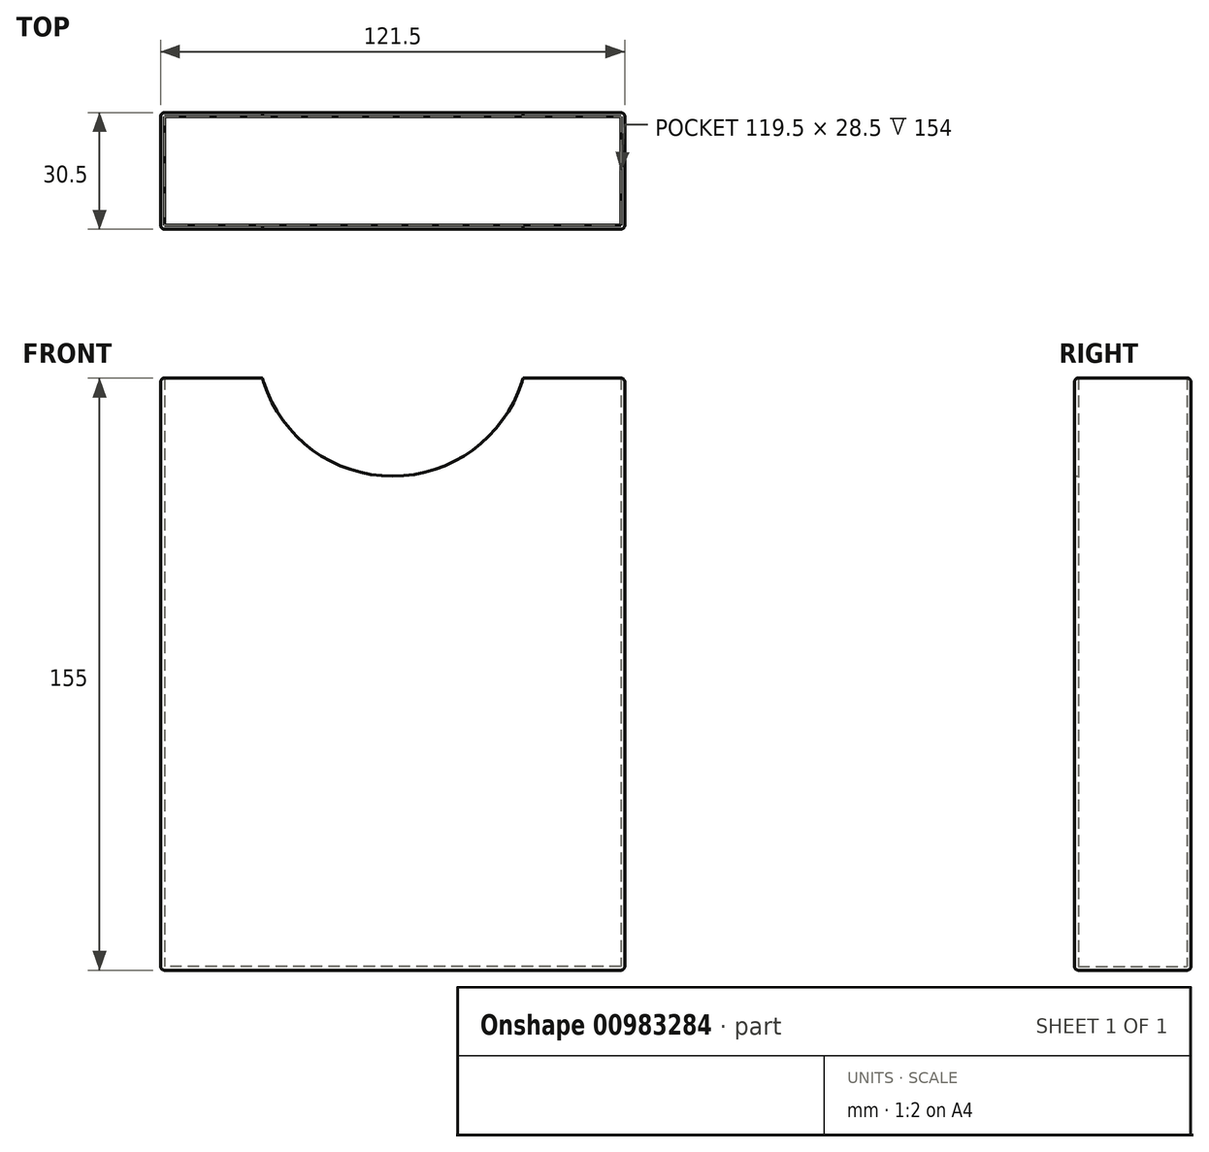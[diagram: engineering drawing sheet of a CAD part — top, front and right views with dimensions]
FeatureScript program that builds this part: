
annotation { "Feature Type Name" : "Feature", "Feature Type Description" : "" }
export const myFeature = defineFeature(function(context is Context, id is Id, definition is map)
    precondition{}
    {
        {
            var Q0;
            Q0=qCreatedBy(makeId("Top.planeOp"),FACE);
            var sketch = newSketch(context, id + "F0", { "sketchPlane" : qUnion([Q0])});
            skPoint(sketch, "E0.middle", {"position": v(0, 0) * mm});
            skLineSegment(sketch, "E1.0", {"start": v(67, -14.5) * mm, "end": v(-52.5, -14.5) * mm});
            skLineSegment(sketch, "E1.1", {"start": v(67, -14.5) * mm, "end": v(67, 14) * mm});
            skLineSegment(sketch, "E1.2", {"start": v(67, 14) * mm, "end": v(-52.5, 14) * mm});
            skLineSegment(sketch, "E1.3", {"start": v(-52.5, -14.5) * mm, "end": v(-52.5, 14) * mm});
            skLineSegment(sketch, "E2.0", {"start": v(68, -15.5) * mm, "end": v(-53.5, -15.5) * mm});
            skLineSegment(sketch, "E2.1", {"start": v(68, -15.5) * mm, "end": v(68, 15) * mm});
            skLineSegment(sketch, "E2.2", {"start": v(68, 15) * mm, "end": v(-53.5, 15) * mm});
            skLineSegment(sketch, "E2.3", {"start": v(-53.5, -15.5) * mm, "end": v(-53.5, 15) * mm});
            skSolve(sketch);
        }
        {
            var Q0;
            Q0=makeQuery(id+"F0.imprint","IMPRINT",FACE,{"disambiguationData":[TD([[makeQuery(id+"F0.imprint","IMPRINT",EDGE,{"derivedFrom":sQuery(id+"F0.wireOp",EDGE,"E1.0")}),1.0]])]});
            extrude(context, id + "F1", {"entities" : qUnion([Q0]), "depth" : 155 * mm, "offsetDistance" : 25 * mm});
        }
        {
            var Q0;
            Q0=makeQuery(id+"F0.imprint","IMPRINT",FACE,{"disambiguationData":[TD([[makeQuery(id+"F0.imprint","IMPRINT",EDGE,{"derivedFrom":sQuery(id+"F0.wireOp",EDGE,"E1.0")}),-1.0]])]});
            extrude(context, id + "F2", {"entities" : qUnion([Q0]), "operationType" : NewBodyOperationType.ADD, "depth" : 1 * mm, "offsetDistance" : 25 * mm});
        }
        {
            var Q0;
            Q0=makeQuery(id+"F1.opExtrude","SWEPT_EDGE",EDGE,{"disambiguationData":[OSD([sQuery(id+"F0.wireOp",EDGE,"E2.0"),sQuery(id+"F0.wireOp",EDGE,"E2.1")])]});
            var Q1;
            Q1=makeQuery(id+"F1.opExtrude","SWEPT_EDGE",EDGE,{"disambiguationData":[OSD([sQuery(id+"F0.wireOp",EDGE,"E2.1"),sQuery(id+"F0.wireOp",EDGE,"E2.2")])]});
            var Q2;
            Q2=makeQuery(id+"F1.opExtrude","CAP_EDGE",EDGE,{"disambiguationData":[OSD([sQuery(id+"F0.wireOp",EDGE,"E2.1")])],"isStart":true});
            var Q3;
            Q3=makeQuery(id+"F1.opExtrude","CAP_EDGE",EDGE,{"disambiguationData":[OSD([sQuery(id+"F0.wireOp",EDGE,"E2.2")])],"isStart":true});
            var Q4;
            Q4=makeQuery(id+"F1.opExtrude","CAP_EDGE",EDGE,{"disambiguationData":[OSD([sQuery(id+"F0.wireOp",EDGE,"E2.0")])],"isStart":true});
            var Q5;
            Q5=makeQuery(id+"F1.opExtrude","CAP_EDGE",EDGE,{"disambiguationData":[OSD([sQuery(id+"F0.wireOp",EDGE,"E2.3")])],"isStart":true});
            var Q6;
            Q6=makeQuery(id+"F1.opExtrude","SWEPT_EDGE",EDGE,{"disambiguationData":[OSD([sQuery(id+"F0.wireOp",EDGE,"E2.0"),sQuery(id+"F0.wireOp",EDGE,"E2.3")])]});
            var Q7;
            Q7=makeQuery(id+"F1.opExtrude","SWEPT_EDGE",EDGE,{"disambiguationData":[OSD([sQuery(id+"F0.wireOp",EDGE,"E2.2"),sQuery(id+"F0.wireOp",EDGE,"E2.3")])]});
            var Q8;
            Q8=makeQuery(id+"F1.opExtrude","CAP_EDGE",EDGE,{"disambiguationData":[OSD([sQuery(id+"F0.wireOp",EDGE,"E2.0")])],"isStart":false});
            var Q9;
            Q9=makeQuery(id+"F1.opExtrude","CAP_EDGE",EDGE,{"disambiguationData":[OSD([sQuery(id+"F0.wireOp",EDGE,"E2.3")])],"isStart":false});
            var Q10;
            Q10=makeQuery(id+"F1.opExtrude","CAP_EDGE",EDGE,{"disambiguationData":[OSD([sQuery(id+"F0.wireOp",EDGE,"E2.2")])],"isStart":false});
            var Q11;
            Q11=makeQuery(id+"F1.opExtrude","CAP_EDGE",EDGE,{"disambiguationData":[OSD([sQuery(id+"F0.wireOp",EDGE,"E2.1")])],"isStart":false});
            fillet(context, id + "F3", {"entities" : qUnion([Q0, Q1, Q2, Q3, Q4, Q5, Q6, Q7, Q8, Q9, Q10, Q11]), "radius" : 1 * mm, "tangentPropagation" : true, "allowEdgeOverflow" : false});
        }
        {
            var Q0;
            Q0=makeQuery(id+"F1.opExtrude","SWEPT_FACE",FACE,{"disambiguationData":[OSD([sQuery(id+"F0.wireOp",EDGE,"E2.2")])]});
            var sketch = newSketch(context, id + "F4", { "sketchPlane" : qUnion([Q0])});
            skLineSegment(sketch, "E3", {"start": v(-7.25, 154) * mm, "end": v(-7.25, 164.81) * mm});
            skCircle(sketch, "E4", {"center": v(-7.25, 164.81) * mm, "radius": 35.5 * mm});
            skSolve(sketch);
        }
        {
            var Q0;
            {var subQ0=sQuery(id+"F4.wireOp",EDGE,"E4");var subQ1=sQuery(id+"F0.wireOp",EDGE,"E2.2");var subQ2=makeQuery(id+"F3.opFillet","BLEND_EDGE",EDGE,{"blendedFrom":[makeQuery(id+"F1.opExtrude","CAP_EDGE",EDGE,{"disambiguationData":[OSD([subQ1])],"isStart":false}),makeQuery(id+"F1.opExtrude","SWEPT_FACE",FACE,{"disambiguationData":[OSD([subQ1])]})],"blendedInto":[makeQuery(id+"F1.opExtrude","SWEPT_FACE",FACE,{"disambiguationData":[OSD([subQ1])]})]});var subQ3=makeQuery(id+"F4.imprint","INTERSECT",VERTEX,{"disambiguationData":[OD(0.0)],"derivedFrom":[subQ2,subQ0]});Q0=makeQuery(id+"F4.imprint","IMPRINT",FACE,{"disambiguationData":[TD([[makeQuery(id+"F4.imprint","IMPRINT",EDGE,{"disambiguationData":[TD([[subQ3,-1.0]])],"derivedFrom":subQ0}),1.0]])]});}
            var Q1;
            {var subQ0=sQuery(id+"F4.wireOp",EDGE,"E4");var subQ1=sQuery(id+"F0.wireOp",EDGE,"E2.2");var subQ2=makeQuery(id+"F3.opFillet","BLEND_EDGE",EDGE,{"blendedFrom":[makeQuery(id+"F1.opExtrude","CAP_EDGE",EDGE,{"disambiguationData":[OSD([subQ1])],"isStart":false}),makeQuery(id+"F1.opExtrude","SWEPT_FACE",FACE,{"disambiguationData":[OSD([subQ1])]})],"blendedInto":[makeQuery(id+"F1.opExtrude","SWEPT_FACE",FACE,{"disambiguationData":[OSD([subQ1])]})]});var subQ3=makeQuery(id+"F4.imprint","INTERSECT",VERTEX,{"disambiguationData":[OD(0.0)],"derivedFrom":[subQ2,subQ0]});Q1=makeQuery(id+"F4.imprint","IMPRINT",FACE,{"disambiguationData":[TD([[makeQuery(id+"F4.imprint","IMPRINT",EDGE,{"disambiguationData":[TD([[subQ3,1.0]])],"derivedFrom":subQ0}),1.0]])]});}
            var Q2;
            Q2=makeQuery(id+"F1.opExtrude","SWEPT_FACE",FACE,{"disambiguationData":[OSD([sQuery(id+"F0.wireOp",EDGE,"E2.0")])]});
            extrude(context, id + "F5", {"entities" : qUnion([Q0, Q1]), "operationType" : NewBodyOperationType.REMOVE, "endBound" : BoundingType.UP_TO_SURFACE, "oppositeDirection" : true, "depth" : 25 * mm, "endBoundEntityFace" : qUnion([Q2]), "offsetDistance" : 25 * mm});
        }
    });
